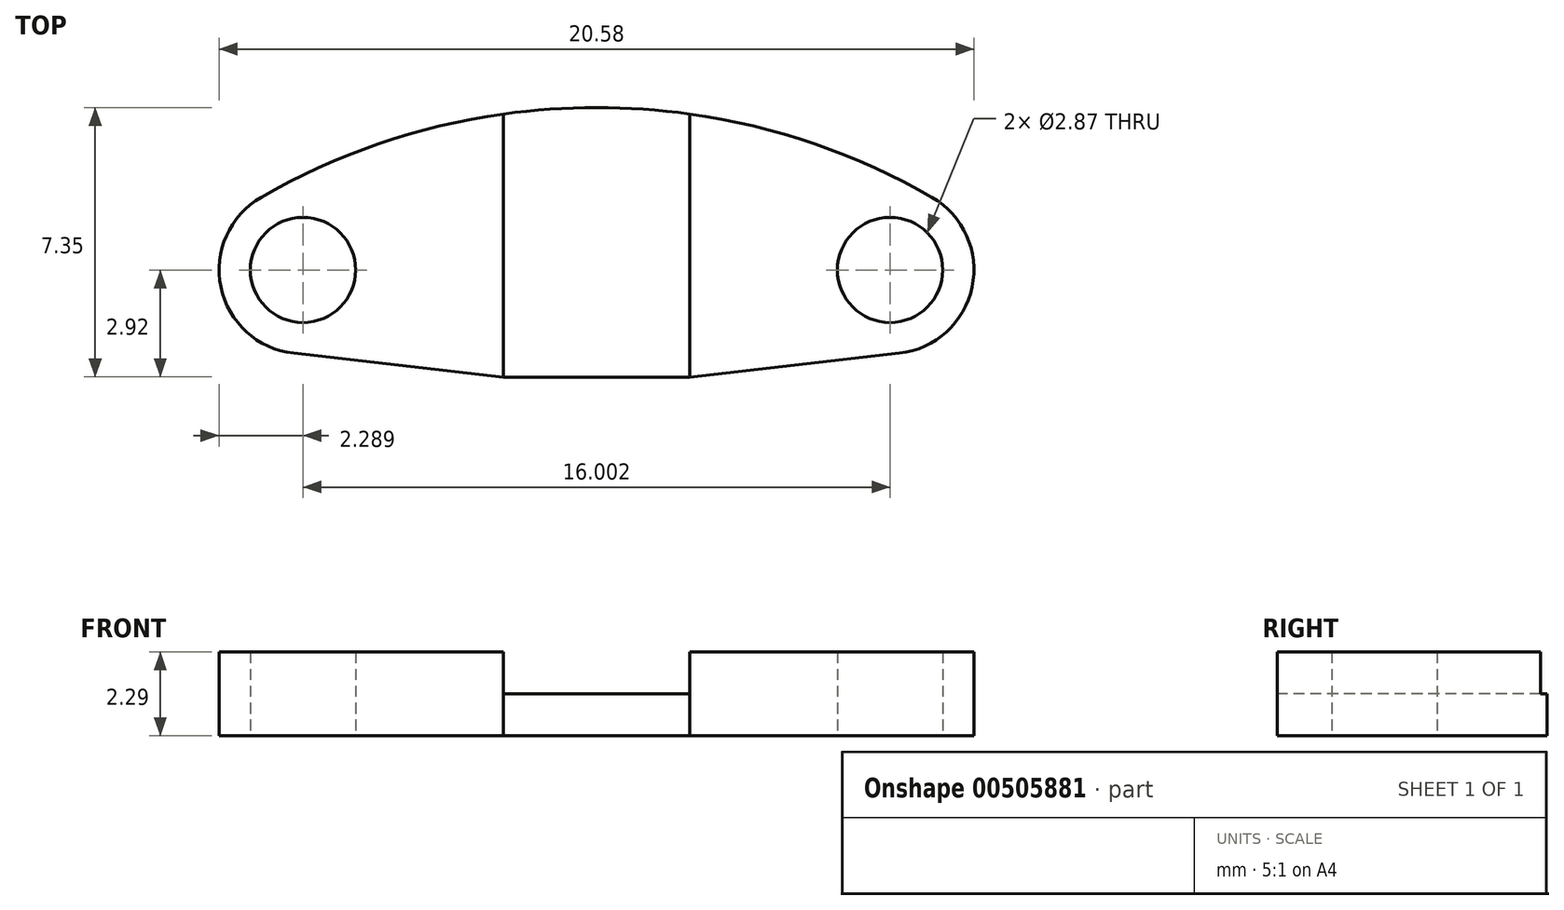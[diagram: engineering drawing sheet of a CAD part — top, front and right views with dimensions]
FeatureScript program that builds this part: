
annotation { "Feature Type Name" : "Feature", "Feature Type Description" : "" }
export const myFeature = defineFeature(function(context is Context, id is Id, definition is map)
    precondition{}
    {
        {
            var Q0;
            Q0=qCreatedBy(makeId("Top.planeOp"),FACE);
            var sketch = newSketch(context, id + "F0", { "sketchPlane" : qUnion([Q0])});
            skArc(sketch, "E0", {"start": v(-9.14, 1.98) * mm, "mid": v(-10.24, -0.47) * mm, "end": v(-8.26, -2.27) * mm});
            skArc(sketch, "E1", {"start": v(8.26, -2.27) * mm, "mid": v(10.24, -0.47) * mm, "end": v(9.14, 1.98) * mm});
            skCircle(sketch, "E2", {"center": v(-8, 0) * mm, "radius": 1.44 * mm});
            skCircle(sketch, "E3", {"center": v(8, 0) * mm, "radius": 1.44 * mm});
            skArc(sketch, "E4", {"start": v(9.14, 1.98) * mm, "mid": v(0, 4.43) * mm, "end": v(-9.14, 1.98) * mm});
            skLineSegment(sketch, "E5", {"start": v(-2.54, -2.92) * mm, "end": v(2.54, -2.92) * mm});
            skLineSegment(sketch, "E6", {"start": v(-2.54, 4.25) * mm, "end": v(-2.54, -2.92) * mm});
            skLineSegment(sketch, "E7", {"start": v(2.54, 4.25) * mm, "end": v(2.54, -2.92) * mm});
            skLineSegment(sketch, "E8", {"start": v(-8.26, -2.27) * mm, "end": v(-2.54, -2.92) * mm});
            skLineSegment(sketch, "E9", {"start": v(2.54, -2.92) * mm, "end": v(8.26, -2.27) * mm});
            skSolve(sketch);
        }
        {
            var Q0;
            Q0 = qSketchRegion(id + "F0", true);
            extrude(context, id + "F1", {"entities" : qUnion([Q0]), "depth" : 2.3 * mm});
        }
        {
            var Q0;
            Q0=makeQuery(id+"F1.opExtrude","CAP_FACE",FACE,{"disambiguationData":[OSD([sQuery(id+"F0.wireOp",EDGE,"E0"),sQuery(id+"F0.wireOp",EDGE,"E1"),sQuery(id+"F0.wireOp",EDGE,"E2"),sQuery(id+"F0.wireOp",EDGE,"E3"),sQuery(id+"F0.wireOp",EDGE,"E4"),sQuery(id+"F0.wireOp",EDGE,"E5"),sQuery(id+"F0.wireOp",EDGE,"E8"),sQuery(id+"F0.wireOp",EDGE,"E9")])],"isStart":false});
            var sketch = newSketch(context, id + "F2", { "sketchPlane" : qUnion([Q0])});
            skLineSegment(sketch, "E10.bottom", {"start": v(-2.54, 5.59) * mm, "end": v(2.54, 5.59) * mm});
            skLineSegment(sketch, "E10.top", {"start": v(-2.54, -5.03) * mm, "end": v(2.54, -5.03) * mm});
            skLineSegment(sketch, "E10.left", {"start": v(-2.54, 5.59) * mm, "end": v(-2.54, -5.03) * mm});
            skLineSegment(sketch, "E10.right", {"start": v(2.54, 5.59) * mm, "end": v(2.54, -5.03) * mm});
            skSolve(sketch);
        }
        {
            var Q0;
            Q0 = qSketchRegion(id + "F2", true);
            extrude(context, id + "F3", {"entities" : qUnion([Q0]), "operationType" : NewBodyOperationType.REMOVE, "oppositeDirection" : true, "depth" : 1.14 * mm});
        }
    });
